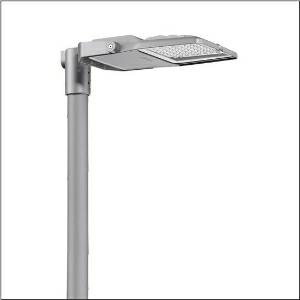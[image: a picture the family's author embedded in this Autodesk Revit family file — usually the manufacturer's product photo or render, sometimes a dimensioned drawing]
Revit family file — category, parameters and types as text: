
# Revit family: floodlight_fl_21_iq_mini___pl52_5xa7771b4d3a_0091
name_source: partatom
category: Lighting Fixtures
units: mm (PartAtom-declared; Revit-internal decimal feet)

## family parameters
Cut with Voids When Loaded = No
Host = Face
Light Source = No
Part Type = Normal
Room Calculation Point = No
Round Connector Dimension = Use Diameter
Shared = No

## types (1)
- --- (1 x LED, 6490 lm, 45.5 W, 4000K)
    Apparent Load = 46 VA
    CIE Flux Codes = 26 60 98 100 100
    Color Rendering = 70
    Color Temperature = 4000K
    Default Elevation = 1800 mm
    Description = Floodlight FL 21 iQ mini, floodlight, primary light control with lens, of PMMA, primary optical cover: protective disc, of toughened safety glass, transparent, light distribution: PL52, light emission: direct distribution, installation type: surface-mounted, LED, High Power LED, rated luminous flux: 6.490lm, luminous efficacy: 143lm/W, light colour: 740, colour temperature: 4000K, control gear: iQ Comfort/DALI, control: Auto-Match, Temp-Guard, Lumen-Switch, Night-Set, Smart-Wire, Light-Fading, Desk-Remote (wireless, voltage-free reading and setting of iQ features in the workshop via application-optimized NFC function/RFID function), optimised constant luminous flux control (CLO 2.0), with terminal, 6-pole, mains connection: 220..240V, AC, 50/60Hz, start of lifetime: 46W, end of service life: 48W, reduction: 22W, luminaire housing, of diecast aluminium, powder-coated, Siteco® metallic grey (DB 702S), corrosivity category C5 mid according to DIN EN ISO 12944, suitable for swimming pools, chlorine-resistant, sealing non-destructively replaceable, please order mast flange separately, mast bracket, of steel, galvanised, powder-coated, Siteco® metallic grey (DB 702S), protection rating (complete): IP66, insulation class (complete): insulation class II (safety insulation), certification: CE, ENEC, VDE, protection symbol: D, impact resistance: IK08, permissible operating ambient temperature: -40..+40°C, permissible operating ambient temperature for outdoor applications: -40..+50°C, standard: DIN EN 12944, LABS conformity tested according to VDMA 24364:2018-05, packaging unit: 1 piece

Light Distribution: PL52
    Height = 70 mm
    Lamp = 1 x LED
    Lamp Light Flux = 6490 lm
    Lamp Power = 45.5 W
    Lamp count = 1
    Length = 485 mm
    Luminous efficacy = 143 lm/W
    Manufacturer = Siteco
    ModVariant = No
    Model = 5XA7771B4D3A
    Number of Poles = 1
    OnlyDefault = Yes
    Power Factor = 1
    Product Name = Floodlight FL 21 iQ mini | PL52
    Product group = floodlight | pylon annexe
    ProductGroupID = 6201
    Protection Class = Protection class II
    Protection Degree = IP 66
    RLX_Detail_Level = 1
    RLX_Emergency_Light_Flux = 0 lm
    RLX_Emergency_Type = 0
    RLX_Emergency_Type_DB = No
    RlxData = <blob elided: 101489 chars, md5=bb8489a4>
    Socket = socket
    Standby Power = 0 W
    System Light Flux = 6490 lm
    System Power = 46 W
    Type Comments = factory setting: luminous flux: 100 % | dim-lin: 254 | 463 mA
    Type Image = l_1007125.jpg
    URL = http://relux.com
    VarID = @adj_186445
    Voltage = 0 V
    Weight = 0.00 kg
    Width = 337 mm

## geometry (parser evidence)
native form markers: Blend x4, Sweep x12
no freeform markers — native parametric forms only
